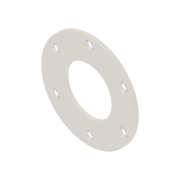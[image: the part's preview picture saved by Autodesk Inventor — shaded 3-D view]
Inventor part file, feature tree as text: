
AUTODESK INVENTOR PART (.ipt)
format: ipt  version: 2011 (Build 150239000, 239)  size: 85,504 bytes
history: native  units: in
note: dims shown in document units (in); Inventor stores cm internally (conversion verified against a paired STEP export)
features: extrude x1, sketch x1
ambient origin geometry x8: Origin, YZ Plane, XZ Plane, XY Plane, X Axis, Y Axis, Z Axis, Center Point
bodies: Solid1 (feature_tree)
feature tree (2):
  extrude  "Extrusion1"  [1 undecoded]
  sketch  "Sketch1"  dims[d0=0.0938in d1=0.0in]
note: 1 required parameter value undecoded (feature->parameter linkage not recoverable at this tier; creation-order binding heuristic only, values carry confidence <= 0.55)
